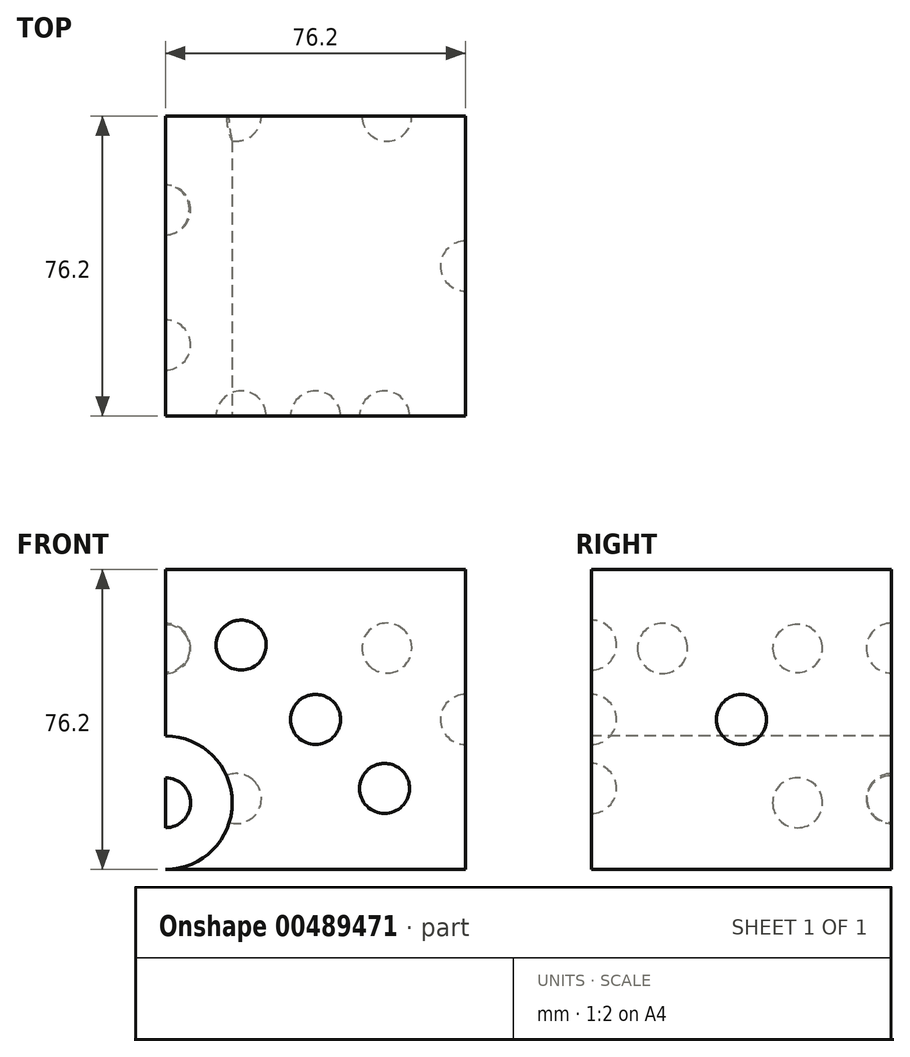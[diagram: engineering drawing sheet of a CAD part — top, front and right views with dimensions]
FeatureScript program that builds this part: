
annotation { "Feature Type Name" : "Feature", "Feature Type Description" : "" }
export const myFeature = defineFeature(function(context is Context, id is Id, definition is map)
    precondition{}
    {
        {
            var Q0;
            Q0=qCreatedBy(makeId("Right.planeOp"),FACE);
            var sketch = newSketch(context, id + "F0", { "sketchPlane" : qUnion([Q0])});
            skLineSegment(sketch, "E0", {"start": v(0, 0) * mm, "end": v(0, 76.2) * mm});
            skLineSegment(sketch, "E1", {"start": v(0, 76.2) * mm, "end": v(-76.2, 76.2) * mm});
            skLineSegment(sketch, "E2", {"start": v(-76.2, 76.2) * mm, "end": v(-76.2, 0) * mm});
            skLineSegment(sketch, "E3", {"start": v(0, 0) * mm, "end": v(-76.2, 0) * mm});
            skSolve(sketch);
        }
        {
            var Q0;
            Q0 = qSketchRegion(id + "F0", true);
            extrude(context, id + "F1", {"entities" : qUnion([Q0]), "depth" : 76.2 * mm});
        }
        {
            var Q0;
            Q0=makeQuery(id+"F1.opExtrude","CAP_FACE",FACE,{"disambiguationData":[OSD([sQuery(id+"F0.wireOp",EDGE,"E0"),sQuery(id+"F0.wireOp",EDGE,"E1"),sQuery(id+"F0.wireOp",EDGE,"E2"),sQuery(id+"F0.wireOp",EDGE,"E3")])],"isStart":false});
            var sketch = newSketch(context, id + "F2", { "sketchPlane" : qUnion([Q0])});
            skArc(sketch, "E4", {"start": v(-38.1, 31.75) * mm, "mid": v(-31.75, 38.1) * mm, "end": v(-38.1, 44.45) * mm});
            skLineSegment(sketch, "E5", {"start": v(-38.1, 76.2) * mm, "end": v(-38.1, 0) * mm});
            skSolve(sketch);
        }
        {
            var Q0;
            Q0 = qSketchRegion(id + "F2", true);
            var Q1;
            Q1=sQuery(id+"F2.wireOp",EDGE,"E5");
            revolve(context, id + "F3", {"operationType" : NewBodyOperationType.REMOVE, "entities" : qUnion([Q0]), "axis" : qUnion([Q1]), "revolveType" : RevolveType.FULL, "oppositeDirection" : true});
        }
        {
            var Q0;
            Q0=makeQuery(id+"F1.opExtrude","SWEPT_FACE",FACE,{"disambiguationData":[OSD([sQuery(id+"F0.wireOp",EDGE,"E0")])]});
            var sketch = newSketch(context, id + "F4", { "sketchPlane" : qUnion([Q0])});
            skLineSegment(sketch, "E6", {"start": v(-76.2, 76.2) * mm, "end": v(0, 0) * mm});
            skArc(sketch, "E7", {"start": v(-51.73, 51.73) * mm, "mid": v(-51.73, 60.7) * mm, "end": v(-60.7, 60.7) * mm});
            skArc(sketch, "E8", {"start": v(-13.5, 13.5) * mm, "mid": v(-13.5, 22.48) * mm, "end": v(-22.48, 22.48) * mm});
            skSolve(sketch);
        }
        {
            var Q0;
            Q0 = qSketchRegion(id + "F4", true);
            var Q1;
            Q1=sQuery(id+"F4.wireOp",EDGE,"E6");
            revolve(context, id + "F5", {"operationType" : NewBodyOperationType.REMOVE, "entities" : qUnion([Q0]), "axis" : qUnion([Q1]), "revolveType" : RevolveType.FULL, "oppositeDirection" : true});
        }
        {
            var Q0;
            Q0=makeQuery(id+"F1.opExtrude","SWEPT_FACE",FACE,{"disambiguationData":[OSD([sQuery(id+"F0.wireOp",EDGE,"E2")])]});
            var sketch = newSketch(context, id + "F6", { "sketchPlane" : qUnion([Q0])});
            skLineSegment(sketch, "E9", {"start": v(0, 76.2) * mm, "end": v(76.2, 0) * mm});
            skArc(sketch, "E10", {"start": v(42.6, 33.6) * mm, "mid": v(42.6, 42.6) * mm, "end": v(33.6, 42.6) * mm});
            skArc(sketch, "E11", {"start": v(23.7, 52.5) * mm, "mid": v(23.7, 61.48) * mm, "end": v(14.72, 61.48) * mm});
            skArc(sketch, "E12", {"start": v(60.12, 16.08) * mm, "mid": v(60.12, 25.06) * mm, "end": v(51.14, 25.06) * mm});
            skSolve(sketch);
        }
        {
            var Q0;
            Q0 = qSketchRegion(id + "F6", true);
            var Q1;
            Q1=sQuery(id+"F6.wireOp",EDGE,"E9");
            revolve(context, id + "F7", {"operationType" : NewBodyOperationType.REMOVE, "entities" : qUnion([Q0]), "axis" : qUnion([Q1]), "revolveType" : RevolveType.FULL, "oppositeDirection" : true});
        }
        {
            var Q0;
            Q0=makeQuery(id+"F1.opExtrude","CAP_FACE",FACE,{"disambiguationData":[OSD([sQuery(id+"F0.wireOp",EDGE,"E0"),sQuery(id+"F0.wireOp",EDGE,"E1"),sQuery(id+"F0.wireOp",EDGE,"E2"),sQuery(id+"F0.wireOp",EDGE,"E3")])],"isStart":true});
            var sketch = newSketch(context, id + "F8", { "sketchPlane" : qUnion([Q0])});
            skPoint(sketch, "E13.end.orphan", {"position": v(76.2, 38.1) * mm});
            skPoint(sketch, "E13.start.orphan", {"position": v(0, 38.1) * mm});
            skPoint(sketch, "E14.endSnap0", {"position": v(53.68, 67.28) * mm});
            skLineSegment(sketch, "E15", {"start": v(0, 16.93) * mm, "end": v(76.2, 16.93) * mm});
            skLineSegment(sketch, "E16", {"start": v(0, 56.15) * mm, "end": v(76.2, 56.15) * mm});
            skCircle(sketch, "E17", {"center": v(23.84, 16.93) * mm, "radius": 6.35 * mm});
            skCircle(sketch, "E18", {"center": v(23.84, 56.37) * mm, "radius": 6.35 * mm});
            skCircle(sketch, "E19", {"center": v(58.16, 56.15) * mm, "radius": 6.35 * mm});
            skCircle(sketch, "E20", {"center": v(58.16, 16.93) * mm, "radius": 6.35 * mm});
            skLineSegment(sketch, "E21.trimOffspring", {"start": v(23.84, 56.15) * mm, "end": v(23.84, 56.37) * mm});
            skPoint(sketch, "E22.orphan", {"position": v(58.16, 76.2) * mm});
            skSolve(sketch);
        }
        {
            var Q0;
            {var subQ0=sQuery(id+"F8.wireOp",EDGE,"E17");var subQ1=sQuery(id+"F8.wireOp",EDGE,"E15");var subQ2=makeQuery(id+"F8.imprint","INTERSECT",VERTEX,{"disambiguationData":[OD(0.0)],"derivedFrom":[subQ1,subQ0]});Q0=makeQuery(id+"F8.imprint","IMPRINT",FACE,{"disambiguationData":[TD([[makeQuery(id+"F8.imprint","IMPRINT",EDGE,{"disambiguationData":[TD([[subQ2,-1.0]])],"derivedFrom":subQ1}),-1.0]])]});}
            var Q1;
            {var subQ0=sQuery(id+"F8.wireOp",EDGE,"E20");var subQ1=sQuery(id+"F8.wireOp",EDGE,"E15");var subQ2=makeQuery(id+"F8.imprint","INTERSECT",VERTEX,{"disambiguationData":[OD(0.0)],"derivedFrom":[subQ1,subQ0]});Q1=makeQuery(id+"F8.imprint","IMPRINT",FACE,{"disambiguationData":[TD([[makeQuery(id+"F8.imprint","IMPRINT",EDGE,{"disambiguationData":[TD([[subQ2,-1.0]])],"derivedFrom":subQ1}),-1.0]])]});}
            var Q2;
            Q2=sQuery(id+"F8.wireOp",EDGE,"E15");
            revolve(context, id + "F9", {"operationType" : NewBodyOperationType.REMOVE, "entities" : qUnion([Q0, Q1]), "axis" : qUnion([Q2]), "revolveType" : RevolveType.FULL, "oppositeDirection" : true});
        }
        {
            var Q0;
            {var subQ0=sQuery(id+"F8.wireOp",EDGE,"E16");var subQ1=makeQuery(id+"F8.imprint","IMPRINT",VERTEX,{"derivedFrom":subQ0});Q0=makeQuery(id+"F8.imprint","IMPRINT",FACE,{"disambiguationData":[TD([[makeQuery(id+"F8.imprint","IMPRINT",EDGE,{"disambiguationData":[TD([[subQ1,1.0]])],"derivedFrom":subQ0}),-1.0]])]});}
            var Q1;
            {var subQ0=sQuery(id+"F8.wireOp",EDGE,"E19");var subQ1=sQuery(id+"F8.wireOp",EDGE,"E16");var subQ2=makeQuery(id+"F8.imprint","INTERSECT",VERTEX,{"disambiguationData":[OD(0.0)],"derivedFrom":[subQ1,subQ0]});Q1=makeQuery(id+"F8.imprint","IMPRINT",FACE,{"disambiguationData":[TD([[makeQuery(id+"F8.imprint","IMPRINT",EDGE,{"disambiguationData":[TD([[subQ2,-1.0]])],"derivedFrom":subQ1}),-1.0]])]});}
            var Q2;
            Q2=sQuery(id+"F8.wireOp",EDGE,"E16");
            revolve(context, id + "F10", {"operationType" : NewBodyOperationType.REMOVE, "entities" : qUnion([Q0, Q1]), "axis" : qUnion([Q2]), "revolveType" : RevolveType.FULL, "oppositeDirection" : true});
        }
    });
